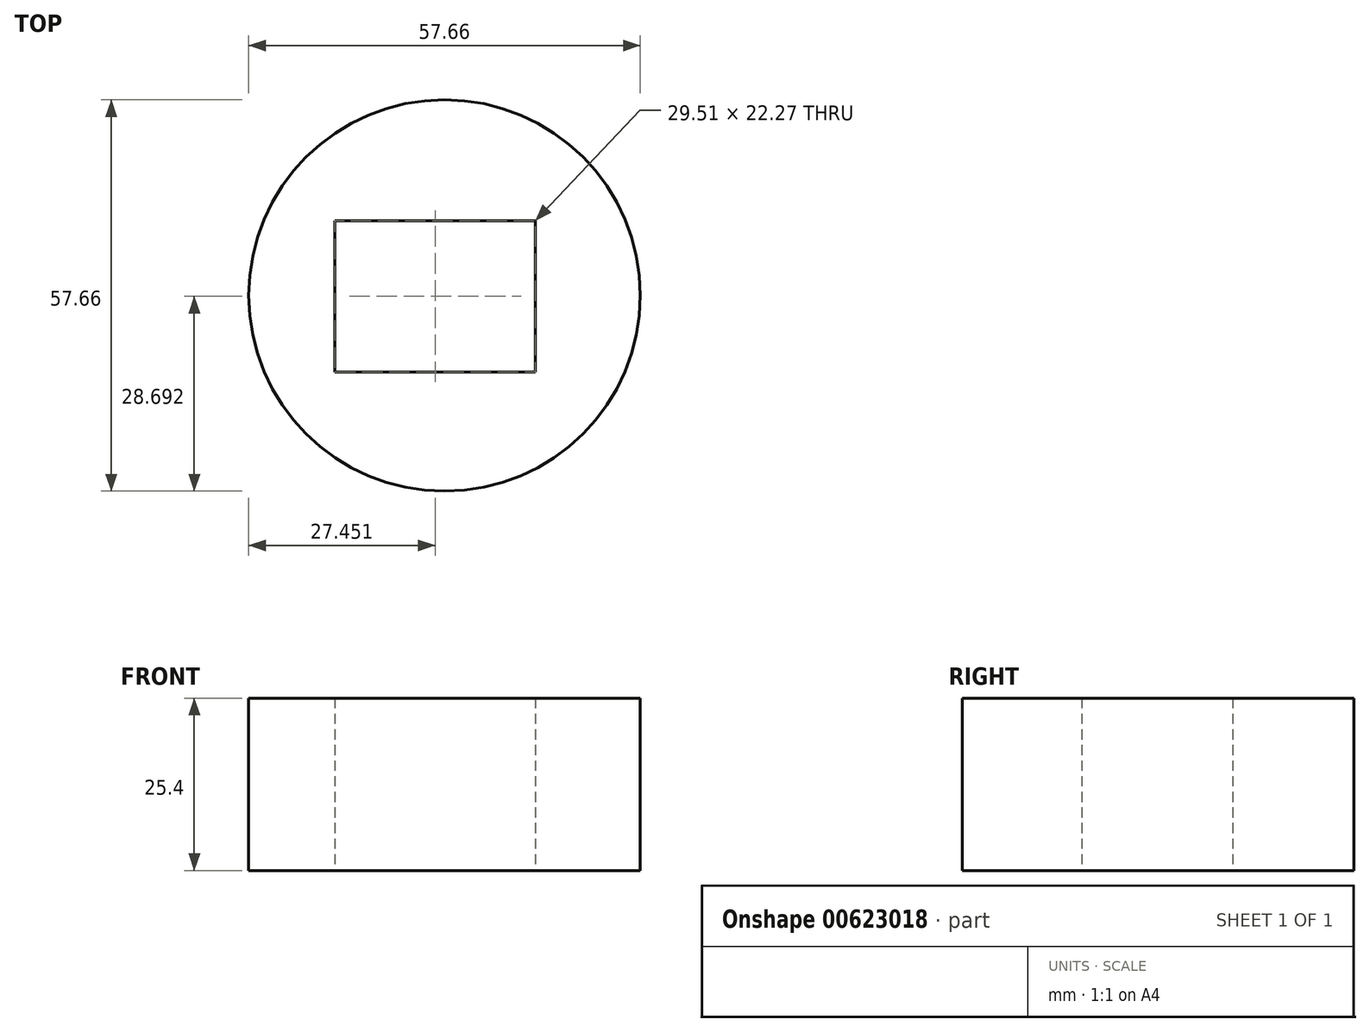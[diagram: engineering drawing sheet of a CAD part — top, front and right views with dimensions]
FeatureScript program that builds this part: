
annotation { "Feature Type Name" : "Feature", "Feature Type Description" : "" }
export const myFeature = defineFeature(function(context is Context, id is Id, definition is map)
    precondition{}
    {
        {
            var Q0;
            Q0=qCreatedBy(makeId("Top.planeOp"),FACE);
            var sketch = newSketch(context, id + "F0", { "sketchPlane" : qUnion([Q0])});
            skCircle(sketch, "E0", {"center": v(0, 0) * mm, "radius": 28.83 * mm});
            skLineSegment(sketch, "E1.bottom", {"start": v(-16.13, 11) * mm, "end": v(13.37, 11) * mm});
            skLineSegment(sketch, "E1.top", {"start": v(-16.13, -11.27) * mm, "end": v(13.37, -11.27) * mm});
            skLineSegment(sketch, "E1.left", {"start": v(-16.13, 11) * mm, "end": v(-16.13, -11.27) * mm});
            skLineSegment(sketch, "E1.right", {"start": v(13.37, 11) * mm, "end": v(13.37, -11.27) * mm});
            skSolve(sketch);
        }
        {
            var Q0;
            Q0=makeQuery(id+"F0.imprint","IMPRINT",FACE,{"disambiguationData":[TD([[makeQuery(id+"F0.imprint","IMPRINT",EDGE,{"derivedFrom":sQuery(id+"F0.wireOp",EDGE,"E0")}),1.0]])]});
            extrude(context, id + "F1", {"entities" : qUnion([Q0]), "depth" : 25.4 * mm, "offsetDistance" : 25.4 * mm});
        }
    });
